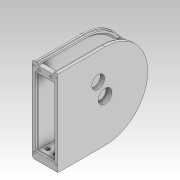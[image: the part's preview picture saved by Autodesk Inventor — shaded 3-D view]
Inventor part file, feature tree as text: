
AUTODESK INVENTOR PART (.ipt)
format: ipt  version: 2020 (Build 240168000, 168)  size: 1,261,056 bytes
history: native  units: mm
features: sketch x51, extrude x48, plane x8, projected_geometry x7, fillet x6, revolve x3, pattern_circular x2, chamfer x2, loft x1, mirror x1, other x1
ambient origin geometry x8: Origin, YZ Plane, XZ Plane, XY Plane, X Axis, Y Axis, Z Axis, Center Point
bodies: Solid1 (feature_tree)
feature tree (130):
  extrude  "Extrusion1"  Depth=250.0mm
  extrude  "Extrusion2"  Depth=100.0mm TaperAngle=0.0deg
  extrude  "Extrusion3"  TaperAngle=0.0deg  [1 undecoded]
  extrude  "Extrusion4"  Depth=10.0mm
  extrude  "Extrusion5"  Depth=1.0mm
  pattern_circular  "Circular Pattern1"  Count=8 Angle=360.0deg
  plane  "Work Plane1"
  plane  "Work Plane2"
  extrude  "Extrusion6"  Depth=30.0mm
  extrude  "Extrusion7"  Depth=10.0mm
  extrude  "Extrusion8"  Depth=10.0mm
  extrude  "Extrusion9"  [1 undecoded]
  chamfer  "Chamfer1"  Distance=10.0mm
  extrude  "Extrusion13"  Depth=10.0mm TaperAngle=0.0deg
  extrude  "Extrusion14"  Depth=3.0mm TaperAngle=0.0deg
  extrude  "Extrusion15"  Depth=2.0mm
  extrude  "Extrusion16"  Depth=3.0mm
  extrude  "Extrusion17"  Depth=80.0mm
  extrude  "Extrusion18"  Depth=60.0mm
  extrude  "Extrusion19"  Depth=80.0mm TaperAngle=360.0deg
  extrude  "Extrusion20"  Depth=15.5mm TaperAngle=0.0deg
  fillet  "Fillet2"  Radius=22.1mm
  pattern_circular  "Circular Pattern2"  Count=8 Angle=360.0deg
  extrude  "Extrusion21"  Depth=10.0mm
  extrude  "Extrusion22"  Depth=7.0mm
  plane  "Work Plane3"
  revolve  "Revolution1"  [1 undecoded]
  revolve  "Revolution2"  [1 undecoded]
  plane  "Work Plane4"
  extrude  "Extrusion23"  Depth=96.8mm TaperAngle=0.0deg
  extrude  "Extrusion24"  Depth=2.5mm
  fillet  "Fillet3"  Radius=5.2mm
  loft  "Loft1"
  extrude  "Extrusion25"  TaperAngle=90.0deg  [1 undecoded]
  extrude  "Extrusion26"  Depth=25.0mm
  extrude  "Extrusion27"  Depth=25.0mm
  extrude  "Extrusion28"  Depth=2.7mm
  plane  "Work Plane5"
  extrude  "Extrusion29"  Depth=5.5mm
  extrude  "Extrusion30"  TaperAngle=90.0deg  [1 undecoded]
  extrude  "Extrusion32"  Depth=2.0mm TaperAngle=0.0deg
  extrude  "Extrusion35"  Depth=6.0mm
  revolve  "Revolution3"  [1 undecoded]
  extrude  "Extrusion36"  [1 undecoded]
  plane  "Work Plane7"
  extrude  "Extrusion37"  Depth=1.0mm TaperAngle=0.0deg
  extrude  "Extrusion38"  Depth=5.0mm
  mirror  "Mirror1"
  extrude  "Extrusion39"  TaperAngle=0.0deg  [1 undecoded]
  extrude  "Extrusion40"  Depth=3.0mm
  extrude  "Extrusion41"  Depth=10.0mm
  chamfer  "Chamfer3"  [1 undecoded]
  fillet  "Fillet5"  [1 undecoded]
  extrude  "Extrusion42"  Depth=255.0mm TaperAngle=0.0deg
  extrude  "Extrusion43"  Depth=65.0mm
  plane  "Work Plane8"
  extrude  "Extrusion44"  Depth=65.0mm TaperAngle=0.0deg
  plane  "Work Plane9"
  extrude  "Extrusion45"  Depth=65.0mm
  extrude  "Extrusion46"  Depth=1.0mm
  fillet  "Fillet8"  Radius=3.0mm
  fillet  "Fillet6"  [1 undecoded]
  fillet  "Fillet7"  Radius=1.0mm
  extrude  "Extrusion47"  TaperAngle=90.0deg  [1 undecoded]
  extrude  "Extrusion48"  Depth=65.0mm
  extrude  "Extrusion49"  Depth=65.0mm
  extrude  "Extrusion50"  Depth=65.0mm TaperAngle=360.0deg
  extrude  "Extrusion51"  Depth=65.0mm TaperAngle=0.0deg
  extrude  "Extrusion52"  Depth=65.0mm
  extrude  "Extrusion53"  Depth=65.0mm TaperAngle=0.0deg
  extrude  "Extrusion54"  Depth=65.0mm
  sketch  "Sketch1"  dims[d0=50.0mm d1=250.0mm]
  sketch  "Sketch2"  dims[d2=50.0mm d3=100.0mm d4=0.0mm]
  sketch  "Sketch4"  dims[d5=5.0mm d7=0.0mm d8=0.0mm]
  sketch  "Sketch5"  dims[d11=10.0mm d12=0.0mm d14=85.0mm]
  sketch  "Sketch7"  dims[d15=1.0mm d16=0.0mm d17=30.0mm]
  projected_geometry  "Projected Loop1"
  sketch  "Sketch8"  dims[d18=3.3mm]
  projected_geometry  "Projected Loop2"
  projected_geometry  "Projected Loop4"
  sketch  "Sketch9"  dims[d19=15.0mm d20=0.0mm d21=80.0mm d22=360.0deg]
  sketch  "Sketch10"  dims[d24=30.0mm d25=30.0mm]
  sketch  "Sketch14"  dims[d30=-5.0mm d31=10.0mm]
  sketch  "Sketch15"  dims[d32=10.0mm d33=10.0mm]
  sketch  "Sketch16"  dims[d34=31.5mm d35=0.0mm d36=-5.0mm d38=10.0mm d39=0.0mm]
  sketch  "Sketch17"  dims[d40=22.1mm d41=10.0mm d42=0.0mm]
  sketch  "Sketch18"  dims[d43=5.0mm d44=3.0mm d45=0.0mm]
  sketch  "Sketch19"  dims[d56=3.0mm d57=2.0mm d58=45.0deg d62=95.1mm]
  sketch  "Sketch20"  dims[d63=10.0mm d64=0.0mm d65=3.0mm]
  sketch  "Sketch21"  dims[d66=0.5mm d67=0.0mm d68=80.0mm]
  sketch  "Sketch22"  dims[d69=16.5mm d70=0.0mm d71=60.0mm]
  sketch  "Sketch23"  dims[d72=3.2mm d73=80.0mm d75=360.0deg]
  other  "Work Axis1"
  sketch  "Sketch24"  dims[d77=15.5mm d78=0.0mm d79=15.5mm d80=0.0mm d81=22.1mm]
  projected_geometry  "Projected Loop5"
  projected_geometry  "Projected Loop6"
  sketch  "Sketch26"  dims[d82=0.0mm d83=0.0mm]
  sketch  "Sketch27"  dims[d84=76.0mm]
  sketch  "Sketch28"  dims[d85=0.1mm d86=0.0mm]
  sketch  "Sketch29"  dims[d87=15.0mm]
  sketch  "Sketch30"  dims[d88=2.0mm]
  sketch  "Sketch31"  dims[d89=22.5mm]
  sketch  "Sketch32"  dims[d90=0.8mm d91=0.0mm]
  sketch  "Sketch33"  dims[d92=0.2mm d93=80.0mm d94=360.0deg]
  projected_geometry  "Projected Loop7"
  sketch  "Sketch34"  dims[d96=24.43461mm d97=10.0mm]
  sketch  "Sketch35"  dims[d98=6.1mm d99=7.0mm]
  sketch  "Sketch38"  dims[d100=6.1mm d101=7.0mm]
  sketch  "Sketch41"  dims[d102=5.0mm d103=0.0mm d104=25.0mm]
  sketch  "Sketch42"  dims[d105=16.1mm d106=96.8mm d107=0.0mm]
  sketch  "Sketch43"  dims[d108=0.0mm d109=2.5mm d110=5.2mm]
  sketch  "Sketch44"  dims[d111=1.0mm d112=5.0mm]
  sketch  "Sketch45"  dims[d113=5.2mm d114=90.0deg]
  sketch  "Sketch46"  dims[d115=15.0mm d116=25.0mm]
  sketch  "Sketch47"  dims[d117=25.0mm d118=19.0mm]
  projected_geometry  "Projected Loop8"
  sketch  "Sketch48"  dims[d119=19.0mm d120=2.7mm]
  sketch  "Sketch49"  dims[d122=4.0mm d123=0.0mm d124=5.5mm]
  sketch  "Sketch50"  dims[d125=2.0mm d126=0.0mm d127=90.0deg]
  sketch  "Sketch51"  dims[d128=2.0mm d129=18.8mm d130=0.0mm]
  sketch  "Sketch52"  dims[d131=111.25mm d132=0.0mm d133=6.0mm]
  sketch  "Sketch53"  dims[d134=4.0mm d135=0.0mm d136=1.0mm]
  sketch  "Sketch54"  dims[d137=1.0mm d138=0.0mm d139=-7.0mm]
  sketch  "Sketch55"  dims[d140=1.0mm d141=1.0mm d142=0.0mm]
  sketch  "Sketch56"  dims[d143=7.0mm d144=5.0mm]
  sketch  "Sketch57"  dims[d145=6.0mm d146=0.0mm d147=90.0deg]
  sketch  "Sketch58"  dims[d148=0.0mm d149=90.0deg d150=3.0mm]
  sketch  "Sketch59"  dims[d151=10.0mm d152=0.0mm d155=110.0mm d156=0.0mm d157=0.0mm d159=30.0deg]
  sketch  "Sketch60"  dims[d160=6.0mm d177=255.0mm d178=0.0mm]
  sketch  "Sketch61"  dims[d179=5.0mm d180=2.1mm d181=52.0mm d182=0.0mm d183=16.1mm d184=1.0mm d185=3.0mm d186=30.0deg d187=1.0mm d188=90.0deg d189=60.0mm d190=3.5mm d191=80.0mm d193=360.0deg d195=52.0mm d196=0.0mm d197=8.0mm d198=0.5mm d199=0.0mm d200=6.0mm d201=1.7mm d202=0.0mm d203=15.0mm d204=20.0mm d205=10.0mm d206=0.0mm d207=1.0mm d208=22.0mm d209=2.0mm d210=0.0mm d211=0.0mm d212=2.0mm d213=2.0mm d214=0.0mm d215=2.0mm d216=2.0mm d217=45.0deg d218=3.0mm d219=5.0mm d220=2.0mm d221=0.0mm d223=30.0mm d224=3.5mm d225=32.0mm d226=0.0mm d227=-6.0mm d229=32.0mm d230=0.0mm d231=12.0mm d232=-17.0mm d233=2.0mm d234=3.0mm d235=30.0mm d237=30.0mm d238=10.0mm d240=10.0mm d242=10.0mm d243=11.0mm d244=0.0mm d245=7.0mm d246=102.5mm d247=0.0mm d248=3.0mm d249=1.0mm d250=3.0mm d251=55.0mm d252=0.0mm d253=0.0mm d254=1.3mm d255=1.3mm d256=1.3mm d257=10.5mm d258=2.0mm d259=0.0mm d260=10.0mm d261=0.0mm d262=10.0mm d263=0.0mm d264=2.0mm d265=8.0mm d266=3.0mm d267=3.0mm d268=3.2mm d269=5.0mm d270=0.0mm d271=10.0mm d272=5.0mm d273=8.0mm d274=7.0mm d275=0.0mm d276=2.5mm d277=2.5mm d278=2.0mm d279=5.0mm d280=7.0mm d281=65.0mm d282=0.0mm d283=100.0mm d284=0.0mm]
note: 13 required parameter values undecoded (feature->parameter linkage not recoverable at this tier; creation-order binding heuristic only, values carry confidence <= 0.55)